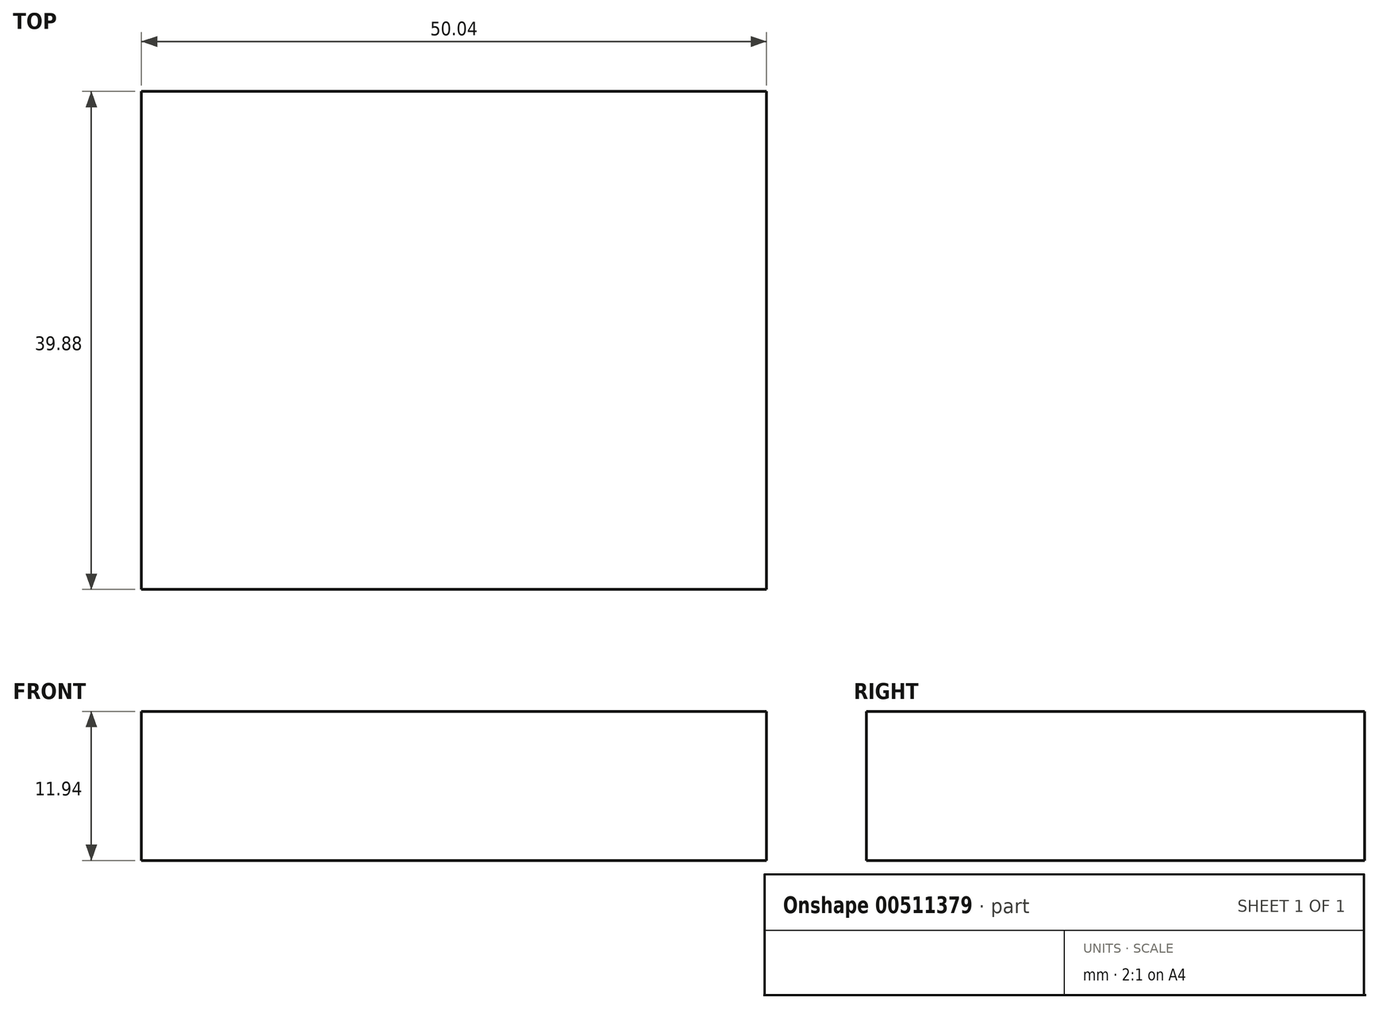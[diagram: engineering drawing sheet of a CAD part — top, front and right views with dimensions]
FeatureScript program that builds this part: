
annotation { "Feature Type Name" : "Feature", "Feature Type Description" : "" }
export const myFeature = defineFeature(function(context is Context, id is Id, definition is map)
    precondition{}
    {
        {
            var Q0;
            Q0=qCreatedBy(makeId("Front.planeOp"),FACE);
            var sketch = newSketch(context, id + "F0", { "sketchPlane" : qUnion([Q0])});
            skLineSegment(sketch, "E0.bottom", {"start": v(-25.02, -5.97) * mm, "end": v(25.02, -5.97) * mm});
            skLineSegment(sketch, "E0.top", {"start": v(-25.02, 5.97) * mm, "end": v(25.02, 5.97) * mm});
            skLineSegment(sketch, "E0.left", {"start": v(-25.02, -5.97) * mm, "end": v(-25.02, 5.97) * mm});
            skLineSegment(sketch, "E0.right", {"start": v(25.02, -5.97) * mm, "end": v(25.02, 5.97) * mm});
            skPoint(sketch, "E0.middle", {"position": v(0, 0) * mm});
            skSolve(sketch);
        }
        {
            var Q0;
            Q0=makeQuery(id+"F0.imprint","IMPRINT",FACE,{"disambiguationData":[TD([[makeQuery(id+"F0.imprint","IMPRINT",EDGE,{"derivedFrom":sQuery(id+"F0.wireOp",EDGE,"E0.bottom")}),1.0]])]});
            extrude(context, id + "F1", {"entities" : qUnion([Q0]), "depth" : 39.88 * mm, "offsetDistance" : 25.4 * mm});
        }
    });
